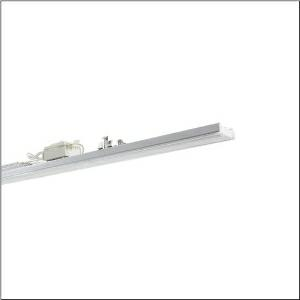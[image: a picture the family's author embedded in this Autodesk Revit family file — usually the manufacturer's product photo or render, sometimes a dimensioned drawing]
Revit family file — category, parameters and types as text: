
# Revit family: licross_11_recessed_ho_51te12dv4m2m3s
name_source: partatom
category: Lighting Fixtures
units: mm (PartAtom-declared; Revit-internal decimal feet)

## family parameters
Cut with Voids When Loaded = No
Host = Face
Light Source = No
Part Type = Normal
Room Calculation Point = No
Round Connector Dimension = Use Diameter
Shared = No

## types (1)
- --- (1 x LED, 1010 lm, 5.9 W, 4000K)
    Apparent Load = 6 VA
    CIE Flux Codes = 66 91 98 100 100
    Color Rendering = 80
    Color Temperature = 4000K
    Default Elevation = 1800 mm
    Description = Licross 11 Recessed HO, luminaire insert, of sheet steel, galvanised, coil coated, white, length: 2.250mm, width: 66mm, height: 67mm, LED rated luminous flux: 27.150lm, light colour: 840, SDCM (Standard Deviation of Colour Matching)MacAdam ≤ 2 SDCM (initial), control gear: DALI 2 (for two DALI lines), with plug, 6-pole, with phase selection, for trunking rail, 14-core, mains connection: 220..240V, AC, 50/60Hz, rated input power: 154W, for trunking rail, 14-core, internal wiring halogen-free, for emergency light function, converter,control gear: single battery element, battery: LiFePO4, 9Ah, primary optical cover: cover, of PMMA, light emission: direct distribution, primary light characteristic: symmetric, protection rating (complete): IP54, insulation class (complete): insulation class I (protective earthing), certification: CE, UKCA, protection symbol: D if used in an environment with non-conductive dust loads with corresponding accessories, impact resistance: IK06, permissible ambient temperature for indoor applications: +5..+35°C, standard: EN 60598-2-22, LABS conformity tested according to VDMA 24364:2018-05, reducing of maximum allowable ambient temperature of 5°C with ceiling mounting, corresponds to IFS (International Featured Standards) requirements for safety and quality in the food industry, The light source and the operating device comply with the requirements of the Ecodesign Regulation (EU) 2019/2020 and are replaceable in accordance with this regulation, packaging unit: 1 piece
    Height = 58 mm
    Lamp = 1 x LED
    Lamp Light Flux = 1010 lm
    Lamp Power = 5.9 W
    Lamp count = 1
    Length = 2250 mm
    Luminous efficacy = 171 lm/W
    Manufacturer = Siteco
    ModVariant = No
    Model = 51TE12DV4M2M3S
    Mounting Place = Ceiling
    Mounting Type = Pendant
    Number of Poles = 1
    OnlyDefault = Yes
    Power Factor = 1
    Product Name = Licross 11 Recessed HO
    Product group = luminaire insert | ceiling pendant
    ProductGroupID = 901
    Protection Class = Protection class I
    Protection Degree = IP 54
    RLX_Detail_Level = 1
    RLX_Emergency_Light_Flux = 0 lm
    RLX_Emergency_Type = 0
    RLX_Emergency_Type_DB = No
    RlxData = <blob elided: 30393 chars, md5=43cac06f>
    Socket = socket
    Standby Power = 0 W
    System Light Flux = 1010 lm
    System Power = 6 W
    Type Comments = : emergency light operation: 3 h
    Type Image = l_1296930.jpg
    URL = http://relux.com
    VarID = @adj_089623
    Voltage = 0 V
    Weight = 0.00 kg
    Width = 66 mm

## geometry (parser evidence)
native form markers: Blend x4, Sweep x10
no freeform markers — native parametric forms only
